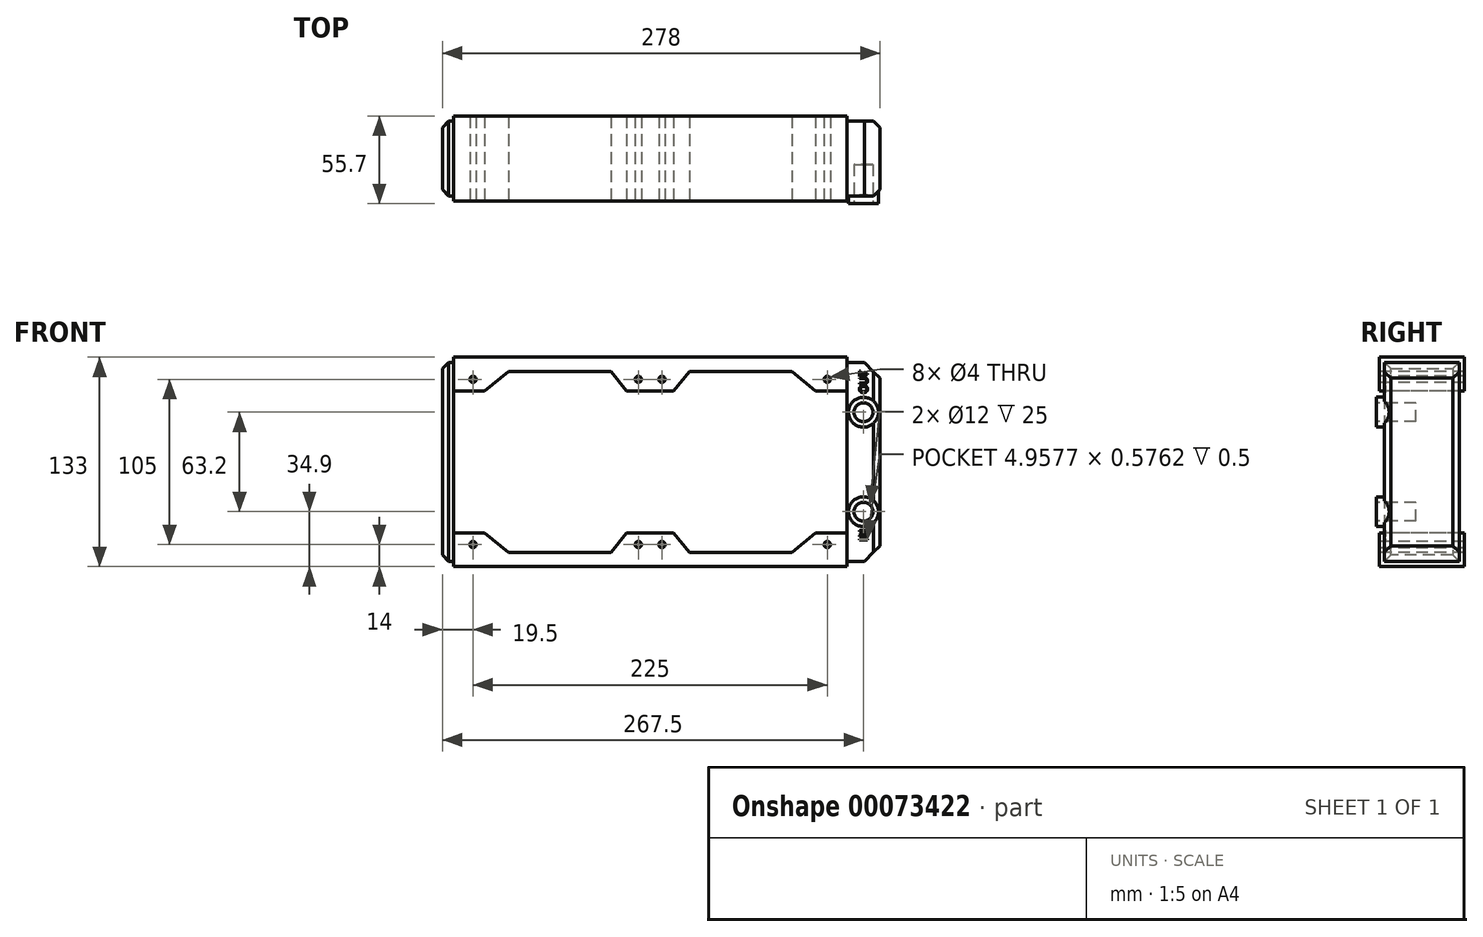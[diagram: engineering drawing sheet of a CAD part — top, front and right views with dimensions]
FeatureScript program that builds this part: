
annotation { "Feature Type Name" : "Feature", "Feature Type Description" : "" }
export const myFeature = defineFeature(function(context is Context, id is Id, definition is map)
    precondition{}
    {
        {
            var Q0;
            Q0=qCreatedBy(makeId("Front.planeOp"),FACE);
            var sketch = newSketch(context, id + "F0", { "sketchPlane" : qUnion([Q0])});
            skLineSegment(sketch, "E0.bottom", {"start": v(0, 63.2) * mm, "end": v(278, 63.2) * mm});
            skLineSegment(sketch, "E0.top", {"start": v(0, -63.2) * mm, "end": v(278, -63.2) * mm});
            skLineSegment(sketch, "E0.left", {"start": v(0, 63.2) * mm, "end": v(0, -63.2) * mm});
            skLineSegment(sketch, "E0.right", {"start": v(278, 63.2) * mm, "end": v(278, -63.2) * mm});
            skPoint(sketch, "E1", {"position": v(0, 0) * mm});
            skSolve(sketch);
        }
        {
            var Q0;
            Q0 = qSketchRegion(id + "F0", true);
            extrude(context, id + "F1", {"entities" : qUnion([Q0]), "depth" : 47.4 * mm});
        }
        {
            var Q0;
            Q0=makeQuery(id+"F1.opExtrude","CAP_FACE",FACE,{"disambiguationData":[OSD([sQuery(id+"F0.wireOp",EDGE,"E0.bottom"),sQuery(id+"F0.wireOp",EDGE,"E0.top"),sQuery(id+"F0.wireOp",EDGE,"E0.left"),sQuery(id+"F0.wireOp",EDGE,"E0.right")])],"isStart":false});
            var sketch = newSketch(context, id + "F2", { "sketchPlane" : qUnion([Q0])});
            skCircle(sketch, "E2", {"center": v(267.5, 31.6) * mm, "radius": 9.5 * mm});
            skCircle(sketch, "E3", {"center": v(267.5, -31.6) * mm, "radius": 9.5 * mm});
            skLineSegment(sketch, "E4", {"start": v(278, 0) * mm, "end": v(0, 0) * mm, "construction": true});
            skSolve(sketch);
        }
        {
            var Q0;
            Q0 = qSketchRegion(id + "F2", true);
            extrude(context, id + "F3", {"entities" : qUnion([Q0]), "operationType" : NewBodyOperationType.ADD, "depth" : 5 * mm});
        }
        {
            var Q0;
            Q0=makeQuery(id+"F3.opExtrude","CAP_FACE",FACE,{"disambiguationData":[OSD([sQuery(id+"F2.wireOp",EDGE,"E2")])],"isStart":false});
            var sketch = newSketch(context, id + "F4", { "sketchPlane" : qUnion([Q0])});
            skCircle(sketch, "E5", {"center": v(267.5, 31.6) * mm, "radius": 6 * mm});
            skCircle(sketch, "E6", {"center": v(267.5, -31.6) * mm, "radius": 6 * mm});
            skSolve(sketch);
        }
        {
            var Q0;
            Q0 = qSketchRegion(id + "F4", true);
            extrude(context, id + "F5", {"entities" : qUnion([Q0]), "operationType" : NewBodyOperationType.REMOVE, "oppositeDirection" : true, "depth" : 25 * mm});
        }
        {
            var Q0;
            Q0=makeQuery(id+"F1.opExtrude","SWEPT_EDGE",EDGE,{"disambiguationData":[OSD([sQuery(id+"F0.wireOp",EDGE,"E0.top"),sQuery(id+"F0.wireOp",EDGE,"E0.right")])]});
            var Q1;
            Q1=makeQuery(id+"F1.opExtrude","SWEPT_EDGE",EDGE,{"disambiguationData":[OSD([sQuery(id+"F0.wireOp",EDGE,"E0.bottom"),sQuery(id+"F0.wireOp",EDGE,"E0.right")])]});
            chamfer(context, id + "F6", {"entities" : qUnion([Q0, Q1]), "width" : 10 * mm, "tangentPropagation" : true});
        }
        {
            var Q0;
            Q0=makeQuery(id+"F1.opExtrude","CAP_EDGE",EDGE,{"disambiguationData":[OSD([sQuery(id+"F0.wireOp",EDGE,"E0.right")])],"isStart":false});
            var Q1;
            Q1=makeQuery(id+"F1.opExtrude","CAP_EDGE",EDGE,{"disambiguationData":[OSD([sQuery(id+"F0.wireOp",EDGE,"E0.right")])],"isStart":true});
            var Q2;
            Q2=makeQuery(id+"F1.opExtrude","CAP_EDGE",EDGE,{"disambiguationData":[OSD([sQuery(id+"F0.wireOp",EDGE,"E0.left")])],"isStart":false});
            var Q3;
            Q3=makeQuery(id+"F1.opExtrude","CAP_EDGE",EDGE,{"disambiguationData":[OSD([sQuery(id+"F0.wireOp",EDGE,"E0.left")])],"isStart":true});
            var Q4;
            Q4=makeQuery(id+"F1.opExtrude","SWEPT_EDGE",EDGE,{"disambiguationData":[OSD([sQuery(id+"F0.wireOp",EDGE,"E0.top"),sQuery(id+"F0.wireOp",EDGE,"E0.left")])]});
            var Q5;
            Q5=makeQuery(id+"F1.opExtrude","SWEPT_EDGE",EDGE,{"disambiguationData":[OSD([sQuery(id+"F0.wireOp",EDGE,"E0.bottom"),sQuery(id+"F0.wireOp",EDGE,"E0.left")])]});
            chamfer(context, id + "F7", {"entities" : qUnion([Q0, Q1, Q2, Q3, Q4, Q5]), "width" : 4 * mm, "tangentPropagation" : true});
        }
        {
            var Q0;
            Q0=makeQuery(id+"F1.opExtrude","SWEPT_FACE",FACE,{"disambiguationData":[OSD([sQuery(id+"F0.wireOp",EDGE,"E0.left")])]});
            cPlane(context, id + "F8", {"entities" : qUnion([Q0]), "cplaneType" : CPlaneType.OFFSET, "offset" : 7 * mm, "oppositeDirection" : true, "width" : 150 * mm, "height" : 150 * mm});
        }
        {
            var Q0;
            Q0=qCreatedBy(id+"F8.planeOp",FACE);
            var sketch = newSketch(context, id + "F9", { "sketchPlane" : qUnion([Q0])});
            skLineSegment(sketch, "E7.bottom", {"start": v(-3.3, 66.5) * mm, "end": v(50.7, 66.5) * mm});
            skLineSegment(sketch, "E7.top", {"start": v(-3.3, -66.5) * mm, "end": v(50.7, -66.5) * mm});
            skLineSegment(sketch, "E7.left", {"start": v(-3.3, 66.5) * mm, "end": v(-3.3, -66.5) * mm});
            skLineSegment(sketch, "E7.right", {"start": v(50.7, 66.5) * mm, "end": v(50.7, -66.5) * mm});
            skLineSegment(sketch, "E8", {"start": v(0, 0) * mm, "end": v(-3.3, 0) * mm, "construction": true});
            skLineSegment(sketch, "E9.bottom", {"start": v(0, 63.2) * mm, "end": v(47.4, 63.2) * mm});
            skLineSegment(sketch, "E9.top", {"start": v(0, -63.2) * mm, "end": v(47.4, -63.2) * mm});
            skLineSegment(sketch, "E9.left", {"start": v(0, 63.2) * mm, "end": v(0, -63.2) * mm});
            skLineSegment(sketch, "E9.right", {"start": v(47.4, 63.2) * mm, "end": v(47.4, -63.2) * mm});
            skSolve(sketch);
        }
        {
            var Q0;
            Q0 = qSketchRegion(id + "F9", true);
            extrude(context, id + "F10", {"entities" : qUnion([Q0]), "oppositeDirection" : true, "depth" : 250 * mm});
        }
        {
            var Q0;
            Q0=makeQuery(id+"F10.opExtrude","SWEPT_FACE",FACE,{"disambiguationData":[OSD([sQuery(id+"F9.wireOp",EDGE,"E7.right")])]});
            var sketch = newSketch(context, id + "F11", { "sketchPlane" : qUnion([Q0])});
            skCircle(sketch, "E10", {"center": v(19.5, 52.5) * mm, "radius": 2 * mm});
            skCircle(sketch, "E11", {"center": v(124.5, 52.5) * mm, "radius": 2 * mm});
            skCircle(sketch, "E12", {"center": v(139.5, 52.5) * mm, "radius": 2 * mm});
            skCircle(sketch, "E13", {"center": v(244.5, 52.5) * mm, "radius": 2 * mm});
            skLineSegment(sketch, "E14", {"start": v(7, 0) * mm, "end": v(257, 0) * mm, "construction": true});
            skLineSegment(sketch, "E15", {"start": v(132, 66.5) * mm, "end": v(132, -66.5) * mm, "construction": true});
            skCircle(sketch, "E16.MirrorC", {"center": v(19.5, -52.5) * mm, "radius": 2 * mm});
            skCircle(sketch, "E17.MirrorC", {"center": v(124.5, -52.5) * mm, "radius": 2 * mm});
            skCircle(sketch, "E18.MirrorC", {"center": v(139.5, -52.5) * mm, "radius": 2 * mm});
            skCircle(sketch, "E19.MirrorC", {"center": v(244.5, -52.5) * mm, "radius": 2 * mm});
            skSolve(sketch);
        }
        {
            var Q0;
            Q0 = qSketchRegion(id + "F11", true);
            extrude(context, id + "F12", {"entities" : qUnion([Q0]), "operationType" : NewBodyOperationType.REMOVE, "endBound" : BoundingType.THROUGH_ALL, "oppositeDirection" : true, "depth" : 25 * mm});
        }
        {
            var Q0;
            Q0=makeQuery(id+"F10.opExtrude","SWEPT_FACE",FACE,{"disambiguationData":[OSD([sQuery(id+"F9.wireOp",EDGE,"E7.right")])]});
            var sketch = newSketch(context, id + "F13", { "sketchPlane" : qUnion([Q0])});
            skLineSegment(sketch, "E20", {"start": v(7, 45) * mm, "end": v(27, 45) * mm});
            skLineSegment(sketch, "E21", {"start": v(27, 45) * mm, "end": v(42, 57.5) * mm});
            skLineSegment(sketch, "E22", {"start": v(42, 57.5) * mm, "end": v(107, 57.5) * mm});
            skLineSegment(sketch, "E23", {"start": v(107, 57.5) * mm, "end": v(117, 45) * mm});
            skLineSegment(sketch, "E24", {"start": v(117, 45) * mm, "end": v(147, 45) * mm});
            skLineSegment(sketch, "E25", {"start": v(147, 45) * mm, "end": v(157, 57.5) * mm});
            skLineSegment(sketch, "E26", {"start": v(157, 57.5) * mm, "end": v(222, 57.5) * mm});
            skLineSegment(sketch, "E27", {"start": v(222, 57.5) * mm, "end": v(237, 45) * mm});
            skLineSegment(sketch, "E28", {"start": v(237, 45) * mm, "end": v(257, 45) * mm});
            skLineSegment(sketch, "E29", {"start": v(257, 45) * mm, "end": v(257, 0) * mm});
            skLineSegment(sketch, "E30", {"start": v(7, 45) * mm, "end": v(7, 0) * mm});
            skLineSegment(sketch, "E31", {"start": v(7, 0) * mm, "end": v(257, 0) * mm, "construction": true});
            skLineSegment(sketch, "E32", {"start": v(132, 66.5) * mm, "end": v(132, 45) * mm, "construction": true});
            skLineSegment(sketch, "E33.MirrorCS", {"start": v(257, -45) * mm, "end": v(257, 0) * mm});
            skLineSegment(sketch, "E34.MirrorCS", {"start": v(237, -45) * mm, "end": v(257, -45) * mm});
            skLineSegment(sketch, "E35.MirrorCS", {"start": v(222, -57.5) * mm, "end": v(237, -45) * mm});
            skLineSegment(sketch, "E36.MirrorCS", {"start": v(157, -57.5) * mm, "end": v(222, -57.5) * mm});
            skLineSegment(sketch, "E37.MirrorCS", {"start": v(147, -45) * mm, "end": v(157, -57.5) * mm});
            skLineSegment(sketch, "E38.MirrorCS", {"start": v(117, -45) * mm, "end": v(147, -45) * mm});
            skLineSegment(sketch, "E39.MirrorCS", {"start": v(107, -57.5) * mm, "end": v(117, -45) * mm});
            skLineSegment(sketch, "E40.MirrorCS", {"start": v(42, -57.5) * mm, "end": v(107, -57.5) * mm});
            skLineSegment(sketch, "E41.MirrorCS", {"start": v(27, -45) * mm, "end": v(42, -57.5) * mm});
            skLineSegment(sketch, "E42.MirrorCS", {"start": v(7, -45) * mm, "end": v(7, 0) * mm});
            skLineSegment(sketch, "E43.MirrorCS", {"start": v(7, -45) * mm, "end": v(27, -45) * mm});
            skSolve(sketch);
        }
        {
            var Q0;
            Q0 = qSketchRegion(id + "F13", true);
            extrude(context, id + "F14", {"entities" : qUnion([Q0]), "operationType" : NewBodyOperationType.REMOVE, "endBound" : BoundingType.THROUGH_ALL, "oppositeDirection" : true, "depth" : 25 * mm});
        }
        {
            var Q0;
            Q0=makeQuery(id+"F1.opExtrude","SWEPT_BODY",BODY,{"disambiguationData":[OSD([sQuery(id+"F0.wireOp",EDGE,"E0.bottom"),sQuery(id+"F0.wireOp",EDGE,"E0.top"),sQuery(id+"F0.wireOp",EDGE,"E0.left"),sQuery(id+"F0.wireOp",EDGE,"E0.right")])]});
            var Q1;
            Q1=makeQuery(id+"F14.boolean.opBoolean","SPLIT",BODY,{"disambiguationData":[OD(0.0)],"derivedFrom":makeQuery(id+"F10.opExtrude","SWEPT_BODY",BODY,{"disambiguationData":[OSD([sQuery(id+"F9.wireOp",EDGE,"E7.bottom"),sQuery(id+"F9.wireOp",EDGE,"E7.top"),sQuery(id+"F9.wireOp",EDGE,"E7.left"),sQuery(id+"F9.wireOp",EDGE,"E7.right"),sQuery(id+"F9.wireOp",EDGE,"E9.bottom"),sQuery(id+"F9.wireOp",EDGE,"E9.top"),sQuery(id+"F9.wireOp",EDGE,"E9.left"),sQuery(id+"F9.wireOp",EDGE,"E9.right")])]})});
            var Q2;
            Q2=makeQuery(id+"F14.boolean.opBoolean","SPLIT",BODY,{"disambiguationData":[OD(1.0)],"derivedFrom":makeQuery(id+"F10.opExtrude","SWEPT_BODY",BODY,{"disambiguationData":[OSD([sQuery(id+"F9.wireOp",EDGE,"E7.bottom"),sQuery(id+"F9.wireOp",EDGE,"E7.top"),sQuery(id+"F9.wireOp",EDGE,"E7.left"),sQuery(id+"F9.wireOp",EDGE,"E7.right"),sQuery(id+"F9.wireOp",EDGE,"E9.bottom"),sQuery(id+"F9.wireOp",EDGE,"E9.top"),sQuery(id+"F9.wireOp",EDGE,"E9.left"),sQuery(id+"F9.wireOp",EDGE,"E9.right")])]})});
            booleanBodies(context, id + "F15", {"operationType" : BooleanOperationType.UNION, "tools" : qUnion([Q0, Q1, Q2])});
        }
        {
            var Q0;
            {var subQ8=sQuery(id+"F0.wireOp",EDGE,"E0.top");var subQ9=sQuery(id+"F0.wireOp",EDGE,"E0.right");var subQ10=sQuery(id+"F0.wireOp",EDGE,"E0.left");var subQ11=sQuery(id+"F0.wireOp",EDGE,"E0.bottom");Q0=makeQuery(id+"F15.opBoolean","SPLIT",FACE,{"disambiguationData":[TD([makeQuery(id+"F1.opExtrude","SWEPT_FACE",FACE,{"disambiguationData":[OSD([subQ11])]})])],"derivedFrom":makeQuery(id+"F1.opExtrude","CAP_FACE",FACE,{"disambiguationData":[OSD([subQ11,subQ8,subQ10,subQ9])],"isStart":false})});}
            var sketch = newSketch(context, id + "F16", { "sketchPlane" : qUnion([Q0])});
            skText(sketch, "E44", { "text": "IN", "fontName": "OpenSans-Regular.ttf"});
            skPoint(sketch, "E45", {"position": v(267.5, -31.6) * mm});
            skPoint(sketch, "E46", {"position": v(267.5, 31.6) * mm});
            skPoint(sketch, "E47", {"position": v(267.5, -43.6) * mm});
            skText(sketch, "E48", { "text": "OUT", "fontName": "OpenSans-Regular.ttf"});
            skPoint(sketch, "E49", {"position": v(267.52, 127.37) * mm});
            skPoint(sketch, "E50", {"position": v(267.5, 43.6) * mm});
            const initialGuessF16  = {"E44": [0.27, -0.05009, 0, 1, 0.005], "E48": [0.27, 0.0436, 0, 1, 0.005]};
            skSetInitialGuess(sketch, initialGuessF16);
            skSolve(sketch);
        }
        {
            var Q0;
            Q0 = qSketchRegion(id + "F16", true);
            extrude(context, id + "F17", {"entities" : qUnion([Q0]), "operationType" : NewBodyOperationType.REMOVE, "oppositeDirection" : true, "depth" : .5 * mm});
        }
    });
